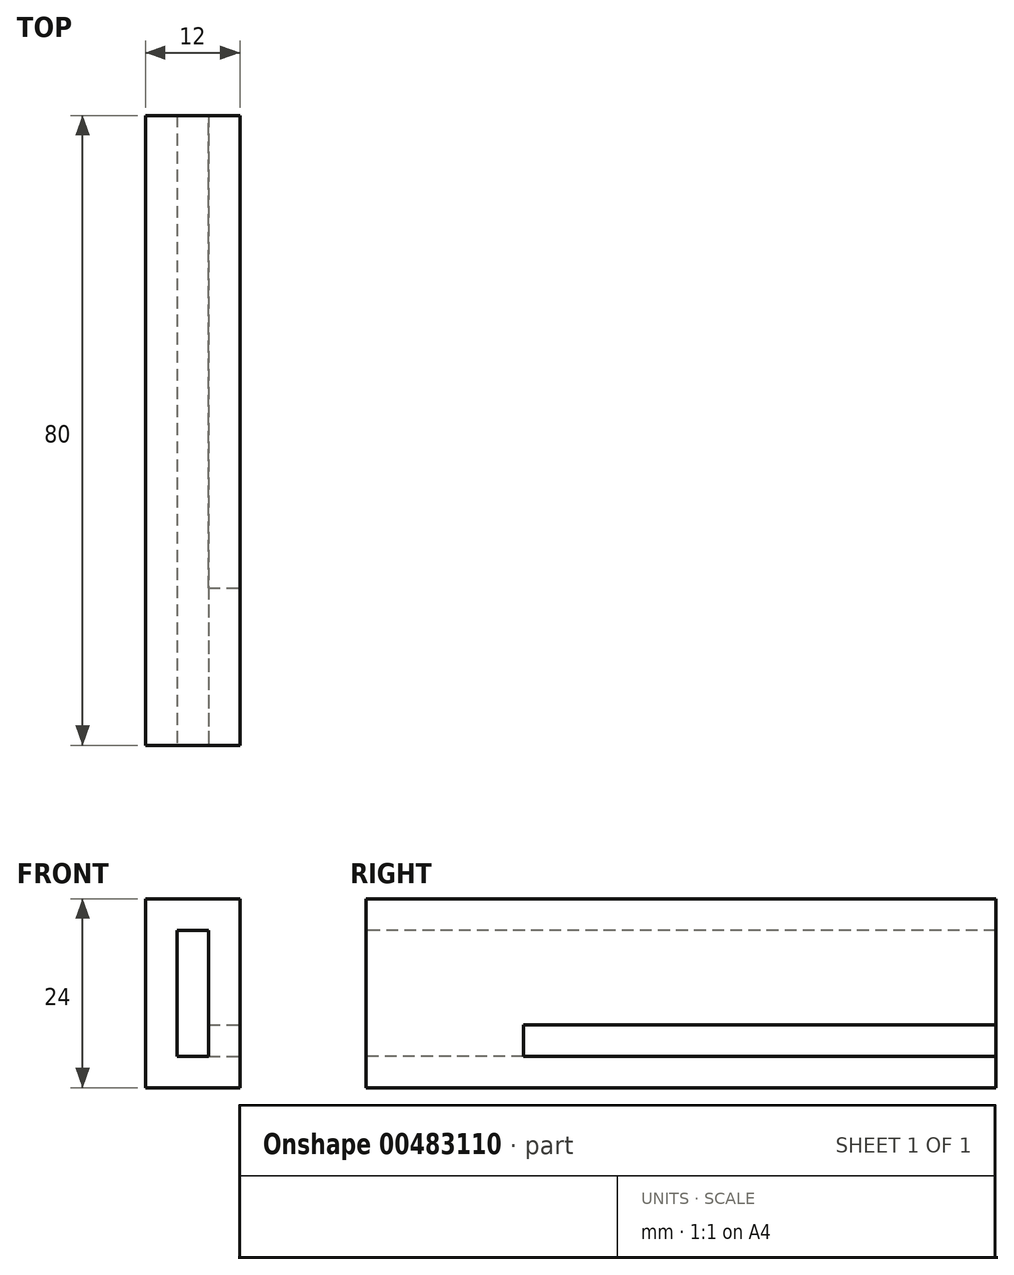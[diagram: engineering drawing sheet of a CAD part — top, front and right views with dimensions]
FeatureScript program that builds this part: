
annotation { "Feature Type Name" : "Feature", "Feature Type Description" : "" }
export const myFeature = defineFeature(function(context is Context, id is Id, definition is map)
    precondition{}
    {
        {
            var Q0;
            Q0=qCreatedBy(makeId("Top.planeOp"),FACE);
            var sketch = newSketch(context, id + "F0", { "sketchPlane" : qUnion([Q0])});
            skLineSegment(sketch, "E0.bottom", {"start": v(0, 0) * mm, "end": v(-12, 0) * mm});
            skLineSegment(sketch, "E0.top", {"start": v(0, 80) * mm, "end": v(-12, 80) * mm});
            skLineSegment(sketch, "E0.left", {"start": v(0, 0) * mm, "end": v(0, 80) * mm});
            skLineSegment(sketch, "E0.right", {"start": v(-12, 0) * mm, "end": v(-12, 80) * mm});
            skSolve(sketch);
        }
        {
            var Q0;
            Q0=makeQuery(id+"F0.imprint","IMPRINT",FACE,{"disambiguationData":[TD([[makeQuery(id+"F0.imprint","IMPRINT",EDGE,{"derivedFrom":sQuery(id+"F0.wireOp",EDGE,"E0.bottom")}),-1.0]])]});
            extrude(context, id + "F1", {"entities" : qUnion([Q0]), "depth" : 24 * mm});
        }
        {
            var Q0;
            Q0=makeQuery(id+"F1.opExtrude","SWEPT_FACE",FACE,{"disambiguationData":[OSD([sQuery(id+"F0.wireOp",EDGE,"E0.bottom")])]});
            var sketch = newSketch(context, id + "F2", { "sketchPlane" : qUnion([Q0])});
            skLineSegment(sketch, "E1.bottom", {"start": v(-8, 20) * mm, "end": v(-4, 20) * mm});
            skLineSegment(sketch, "E1.top", {"start": v(-8, 4) * mm, "end": v(-4, 4) * mm});
            skLineSegment(sketch, "E1.left", {"start": v(-8, 20) * mm, "end": v(-8, 4) * mm});
            skLineSegment(sketch, "E1.right", {"start": v(-4, 20) * mm, "end": v(-4, 4) * mm});
            skSolve(sketch);
        }
        {
            var Q0;
            Q0=makeQuery(id+"F2.imprint","IMPRINT",FACE,{"disambiguationData":[TD([[makeQuery(id+"F2.imprint","IMPRINT",EDGE,{"derivedFrom":sQuery(id+"F2.wireOp",EDGE,"E1.bottom")}),-1.0]])]});
            extrude(context, id + "F3", {"entities" : qUnion([Q0]), "operationType" : NewBodyOperationType.REMOVE, "oppositeDirection" : true, "depth" : 9900 * mm});
        }
        {
            var Q0;
            Q0=makeQuery(id+"F1.opExtrude","SWEPT_FACE",FACE,{"disambiguationData":[OSD([sQuery(id+"F0.wireOp",EDGE,"E0.left")])]});
            var sketch = newSketch(context, id + "F4", { "sketchPlane" : qUnion([Q0])});
            skLineSegment(sketch, "E2.left", {"start": v(80.9, 5.45) * mm, "end": v(80.9, 5.45) * mm});
            skLineSegment(sketch, "E2.right", {"start": v(84.42, 5.45) * mm, "end": v(84.42, 5.45) * mm});
            skLineSegment(sketch, "E3.bottom", {"start": v(20, 8) * mm, "end": v(80, 8) * mm});
            skLineSegment(sketch, "E3.top", {"start": v(20, 4) * mm, "end": v(80, 4) * mm});
            skLineSegment(sketch, "E3.left", {"start": v(20, 8) * mm, "end": v(20, 4) * mm});
            skLineSegment(sketch, "E3.right", {"start": v(80, 8) * mm, "end": v(80, 4) * mm});
            skLineSegment(sketch, "E4", {"start": v(19.09, 0) * mm, "end": v(40, 0) * mm});
            skSolve(sketch);
        }
        {
            var Q0;
            Q0=makeQuery(id+"F4.imprint","IMPRINT",FACE,{"disambiguationData":[TD([[makeQuery(id+"F4.imprint","IMPRINT",EDGE,{"derivedFrom":sQuery(id+"F4.wireOp",EDGE,"E3.bottom")}),-1.0]])]});
            extrude(context, id + "F5", {"entities" : qUnion([Q0]), "operationType" : NewBodyOperationType.REMOVE, "oppositeDirection" : true, "depth" : 4 * mm});
        }
    });
